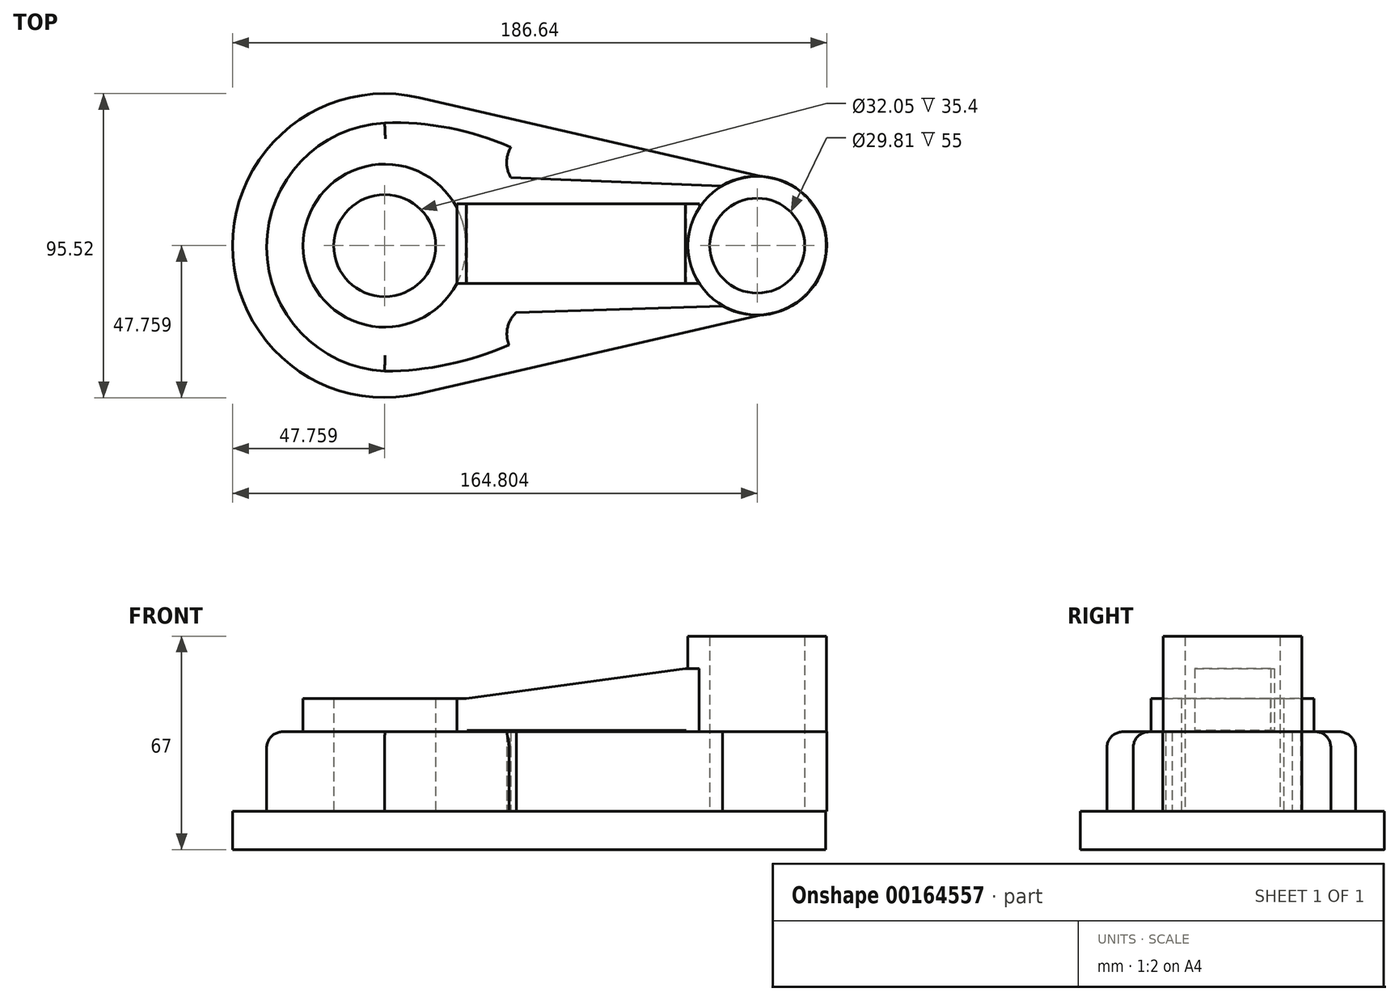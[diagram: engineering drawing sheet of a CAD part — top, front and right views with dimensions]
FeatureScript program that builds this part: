
annotation { "Feature Type Name" : "Feature", "Feature Type Description" : "" }
export const myFeature = defineFeature(function(context is Context, id is Id, definition is map)
    precondition{}
    {
        {
            var Q0;
            Q0=qCreatedBy(makeId("Top.planeOp"),FACE);
            var sketch = newSketch(context, id + "F0", { "sketchPlane" : qUnion([Q0])});
            skLineSegment(sketch, "E0", {"start": v(-36.5, 45.95) * mm, "end": v(-36.5, -47.13) * mm});
            skArc(sketch, "E1", {"start": v(-36.5, 45.95) * mm, "mid": v(-94.96, -0.6) * mm, "end": v(-36.5, -47.13) * mm});
            skLineSegment(sketch, "E2", {"start": v(-36.5, 45.95) * mm, "end": v(74.62, 20.39) * mm});
            skLineSegment(sketch, "E3", {"start": v(-36.5, -47.13) * mm, "end": v(74.67, -21.56) * mm});
            skLineSegment(sketch, "E4", {"start": v(74.62, 20.39) * mm, "end": v(74.67, -21.56) * mm});
            skArc(sketch, "E5", {"start": v(74.67, -21.56) * mm, "mid": v(91.36, -0.57) * mm, "end": v(74.62, 20.39) * mm});
            skSolve(sketch);
        }
        {
            var Q0;
            Q0 = qSketchRegion(id + "F0", true);
            extrude(context, id + "F1", {"entities" : qUnion([Q0]), "depth" : 12 * mm});
        }
        {
            var Q0;
            Q0=makeQuery(id+"F1.opExtrude","CAP_FACE",FACE,{"disambiguationData":[OSD([sQuery(id+"F0.wireOp",EDGE,"E1"),sQuery(id+"F0.wireOp",EDGE,"E2"),sQuery(id+"F0.wireOp",EDGE,"E3"),sQuery(id+"F0.wireOp",EDGE,"E5")])],"isStart":false});
            var sketch = newSketch(context, id + "F2", { "sketchPlane" : qUnion([Q0])});
            skCircle(sketch, "E6", {"center": v(-47.2, -0.6) * mm, "radius": 15.22 * mm});
            skCircle(sketch, "E7", {"center": v(-47.2, -0.6) * mm, "radius": 20.2 * mm});
            skLineSegment(sketch, "E8", {"start": v(-47.2, -40.04) * mm, "end": v(-47.2, 37.97) * mm});
            skArc(sketch, "E9", {"start": v(-47.2, 37.97) * mm, "mid": v(-84.26, -1.03) * mm, "end": v(-47.2, -40.04) * mm});
            skArc(sketch, "E10", {"start": v(-47.2, -40.04) * mm, "mid": v(-27.25, -37.92) * mm, "end": v(-8.16, -31.77) * mm});
            skArc(sketch, "E11", {"start": v(-7.57, 30.29) * mm, "mid": v(-26.94, 36.41) * mm, "end": v(-47.2, 37.97) * mm});
            skArc(sketch, "E12", {"start": v(-5.8, -21.56) * mm, "mid": v(-8.57, -26.3) * mm, "end": v(-8.16, -31.77) * mm});
            skArc(sketch, "E13", {"start": v(-7.57, 30.29) * mm, "mid": v(-8.87, 25.56) * mm, "end": v(-7.57, 20.83) * mm});
            skCircle(sketch, "E14", {"center": v(69.84, -0.6) * mm, "radius": 15.24 * mm});
            skCircle(sketch, "E15", {"center": v(69.84, -0.6) * mm, "radius": 21.84 * mm});
            skLineSegment(sketch, "E16", {"start": v(-5.8, -21.56) * mm, "end": v(58.99, -19.54) * mm});
            skLineSegment(sketch, "E17", {"start": v(-7.57, 20.83) * mm, "end": v(58.63, 18.15) * mm});
            skSolve(sketch);
        }
        {
            var Q0;
            Q0 = qSketchRegion(id + "F2", true);
            extrude(context, id + "F3", {"entities" : qUnion([Q0]), "operationType" : NewBodyOperationType.ADD, "depth" : 25 * mm});
        }
        {
            var Q0;
            Q0=makeQuery(id+"F3.boolean.opBoolean","SPLIT",FACE,{"disambiguationData":[TD([makeQuery(id+"F3.opExtrude","SWEPT_FACE",FACE,{"disambiguationData":[OSD([sQuery(id+"F2.wireOp",EDGE,"E7")])]})])],"derivedFrom":makeQuery(id+"F1.opExtrude","CAP_FACE",FACE,{"disambiguationData":[OSD([sQuery(id+"F0.wireOp",EDGE,"E1"),sQuery(id+"F0.wireOp",EDGE,"E2"),sQuery(id+"F0.wireOp",EDGE,"E3"),sQuery(id+"F0.wireOp",EDGE,"E5")])],"isStart":false})});
            var sketch = newSketch(context, id + "F4", { "sketchPlane" : qUnion([Q0])});
            skCircle(sketch, "E18", {"center": v(-47.2, -0.6) * mm, "radius": 16.03 * mm});
            skCircle(sketch, "E19", {"center": v(-47.2, -0.6) * mm, "radius": 25.61 * mm});
            skSolve(sketch);
        }
        {
            var Q0;
            Q0 = qSketchRegion(id + "F4", true);
            extrude(context, id + "F5", {"entities" : qUnion([Q0]), "operationType" : NewBodyOperationType.ADD, "depth" : 35.4 * mm});
        }
        {
            var Q0;
            Q0=makeQuery(id+"F3.boolean.opBoolean","SPLIT",FACE,{"disambiguationData":[TD([makeQuery(id+"F3.opExtrude","SWEPT_FACE",FACE,{"disambiguationData":[OSD([sQuery(id+"F2.wireOp",EDGE,"E14")])]})])],"derivedFrom":makeQuery(id+"F1.opExtrude","CAP_FACE",FACE,{"disambiguationData":[OSD([sQuery(id+"F0.wireOp",EDGE,"E1"),sQuery(id+"F0.wireOp",EDGE,"E2"),sQuery(id+"F0.wireOp",EDGE,"E3"),sQuery(id+"F0.wireOp",EDGE,"E5")])],"isStart":false})});
            var sketch = newSketch(context, id + "F6", { "sketchPlane" : qUnion([Q0])});
            skCircle(sketch, "E20", {"center": v(69.84, -0.6) * mm, "radius": 14.9 * mm});
            skCircle(sketch, "E21", {"center": v(69.84, -0.6) * mm, "radius": 21.76 * mm});
            skSolve(sketch);
        }
        {
            var Q0;
            Q0 = qSketchRegion(id + "F6", true);
            extrude(context, id + "F7", {"entities" : qUnion([Q0]), "operationType" : NewBodyOperationType.ADD, "depth" : 55 * mm});
        }
        {
            var Q0;
            Q0=qCreatedBy(makeId("Front.planeOp"),FACE);
            var sketch = newSketch(context, id + "F8", { "sketchPlane" : qUnion([Q0])});
            skLineSegment(sketch, "E22", {"start": v(47.85, 56.88) * mm, "end": v(-21.59, 47.43) * mm});
            skLineSegment(sketch, "E23", {"start": v(-21.59, 47.43) * mm, "end": v(-21.59, 37.38) * mm});
            skLineSegment(sketch, "E24", {"start": v(-21.59, 37.38) * mm, "end": v(48.15, 37.38) * mm});
            skLineSegment(sketch, "E25", {"start": v(48.15, 37.38) * mm, "end": v(47.85, 56.88) * mm});
            skSolve(sketch);
        }
        {
            var Q0;
            Q0 = qSketchRegion(id + "F8", true);
            extrude(context, id + "F9", {"entities" : qUnion([Q0]), "operationType" : NewBodyOperationType.ADD, "endBound" : BoundingType.SYMMETRIC, "depth" : 25 * mm});
        }
        {
            var Q0;
            Q0=qCreatedBy(makeId("Front.planeOp"),FACE);
            var sketch = newSketch(context, id + "F10", { "sketchPlane" : qUnion([Q0])});
            skLineSegment(sketch, "E26", {"start": v(-21.59, 47.43) * mm, "end": v(-24.54, 47.43) * mm});
            skLineSegment(sketch, "E27", {"start": v(-24.54, 47.43) * mm, "end": v(-24.54, 37.08) * mm});
            skLineSegment(sketch, "E28", {"start": v(-24.54, 37.08) * mm, "end": v(-21.3, 37.08) * mm});
            skLineSegment(sketch, "E29", {"start": v(-21.3, 37.08) * mm, "end": v(-21.59, 47.43) * mm});
            skLineSegment(sketch, "E30", {"start": v(47.26, 56.88) * mm, "end": v(51.7, 56.88) * mm});
            skLineSegment(sketch, "E31", {"start": v(51.7, 56.88) * mm, "end": v(51.7, 37.08) * mm});
            skLineSegment(sketch, "E32", {"start": v(51.7, 37.08) * mm, "end": v(47.56, 37.08) * mm});
            skLineSegment(sketch, "E33", {"start": v(47.56, 37.08) * mm, "end": v(47.26, 56.88) * mm});
            skSolve(sketch);
        }
        {
            var Q0;
            Q0 = qSketchRegion(id + "F10", true);
            extrude(context, id + "F11", {"entities" : qUnion([Q0]), "operationType" : NewBodyOperationType.ADD, "endBound" : BoundingType.SYMMETRIC, "depth" : 25 * mm});
        }
        {
            var Q0;
            Q0=makeQuery(id+"F3.opExtrude","CAP_EDGE",EDGE,{"disambiguationData":[OSD([sQuery(id+"F2.wireOp",EDGE,"E9")])],"isStart":false});
            var Q1;
            Q1=makeQuery(id+"F3.opExtrude","CAP_EDGE",EDGE,{"disambiguationData":[OSD([sQuery(id+"F2.wireOp",EDGE,"E10")])],"isStart":false});
            var Q2;
            Q2=makeQuery(id+"F3.opExtrude","CAP_EDGE",EDGE,{"disambiguationData":[OSD([sQuery(id+"F2.wireOp",EDGE,"E11")])],"isStart":false});
            fillet(context, id + "F12", {"entities" : qUnion([Q0, Q1, Q2]), "radius" : 5 * mm, "tangentPropagation" : true, "allowEdgeOverflow" : false});
        }
    });
